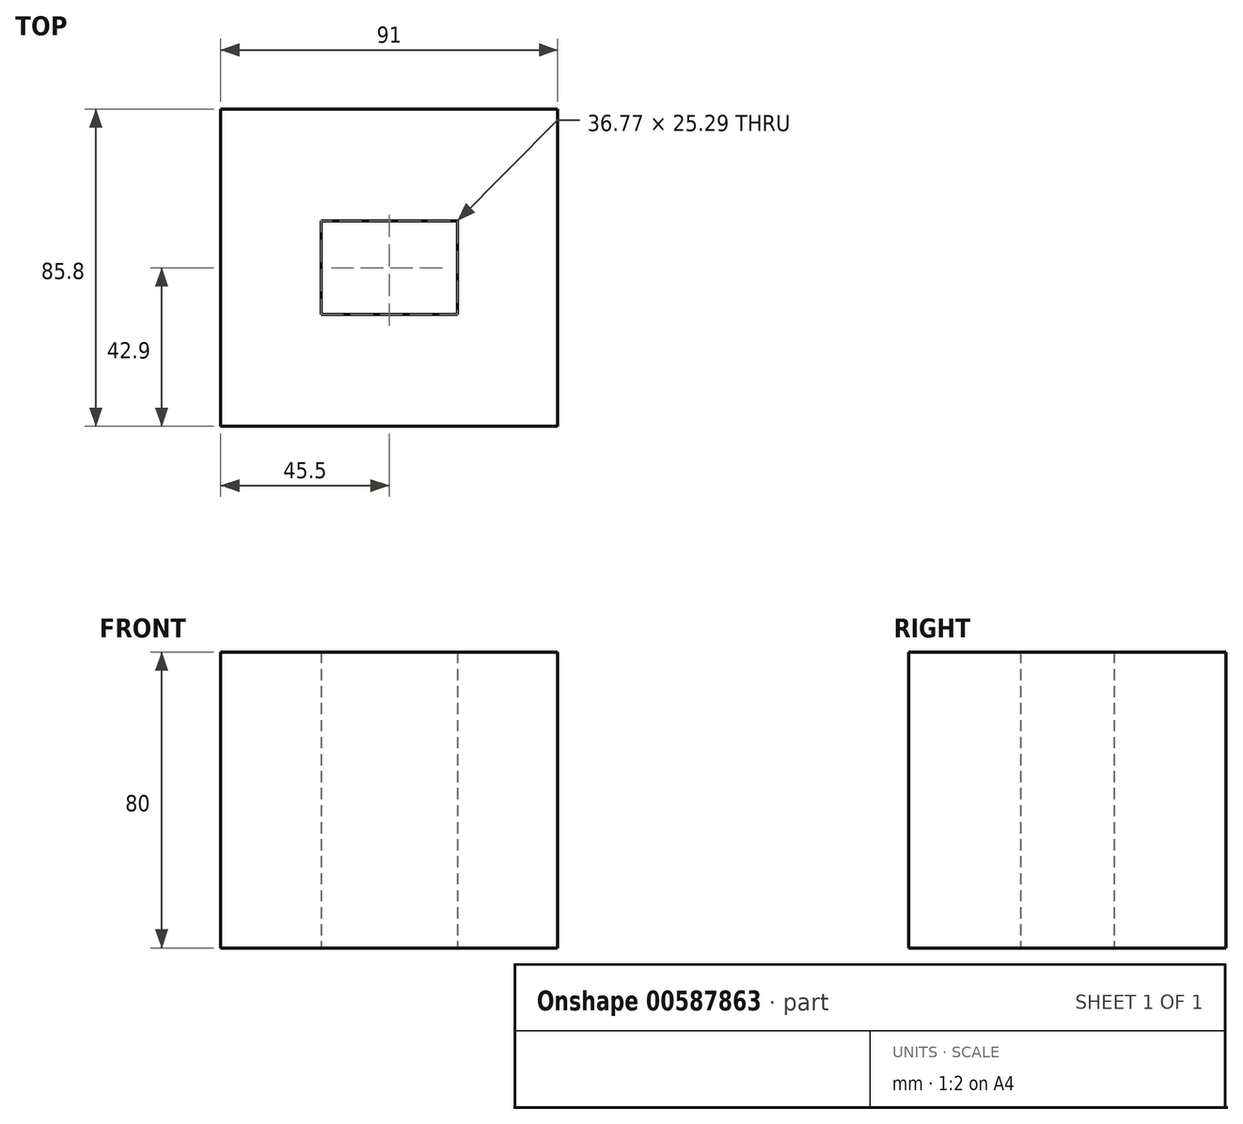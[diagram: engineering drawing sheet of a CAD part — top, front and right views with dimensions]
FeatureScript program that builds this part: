
annotation { "Feature Type Name" : "Feature", "Feature Type Description" : "" }
export const myFeature = defineFeature(function(context is Context, id is Id, definition is map)
    precondition{}
    {
        {
            var Q0;
            Q0=qCreatedBy(makeId("Top.planeOp"),FACE);
            var sketch = newSketch(context, id + "F0", { "sketchPlane" : qUnion([Q0])});
            skLineSegment(sketch, "E0.bottom", {"start": v(45.5, 42.9) * mm, "end": v(-45.5, 42.9) * mm});
            skLineSegment(sketch, "E0.top", {"start": v(45.5, -42.9) * mm, "end": v(-45.5, -42.9) * mm});
            skLineSegment(sketch, "E0.left", {"start": v(45.5, 42.9) * mm, "end": v(45.5, -42.9) * mm});
            skLineSegment(sketch, "E0.right", {"start": v(-45.5, 42.9) * mm, "end": v(-45.5, -42.9) * mm});
            skPoint(sketch, "E0.middle", {"position": v(0, 0) * mm});
            skLineSegment(sketch, "E1.bottom", {"start": v(18.38, 12.65) * mm, "end": v(-18.38, 12.65) * mm});
            skLineSegment(sketch, "E1.top", {"start": v(18.38, -12.65) * mm, "end": v(-18.38, -12.65) * mm});
            skLineSegment(sketch, "E1.left", {"start": v(18.38, 12.65) * mm, "end": v(18.38, -12.65) * mm});
            skLineSegment(sketch, "E1.right", {"start": v(-18.38, 12.65) * mm, "end": v(-18.38, -12.65) * mm});
            skSolve(sketch);
        }
        {
            var Q0;
            Q0=makeQuery(id+"F0.imprint","IMPRINT",FACE,{"disambiguationData":[TD([[makeQuery(id+"F0.imprint","IMPRINT",EDGE,{"derivedFrom":sQuery(id+"F0.wireOp",EDGE,"E0.bottom")}),1.0]])]});
            extrude(context, id + "F1", {"entities" : qUnion([Q0]), "depth" : 80 * mm, "offsetDistance" : 25 * mm});
        }
    });
